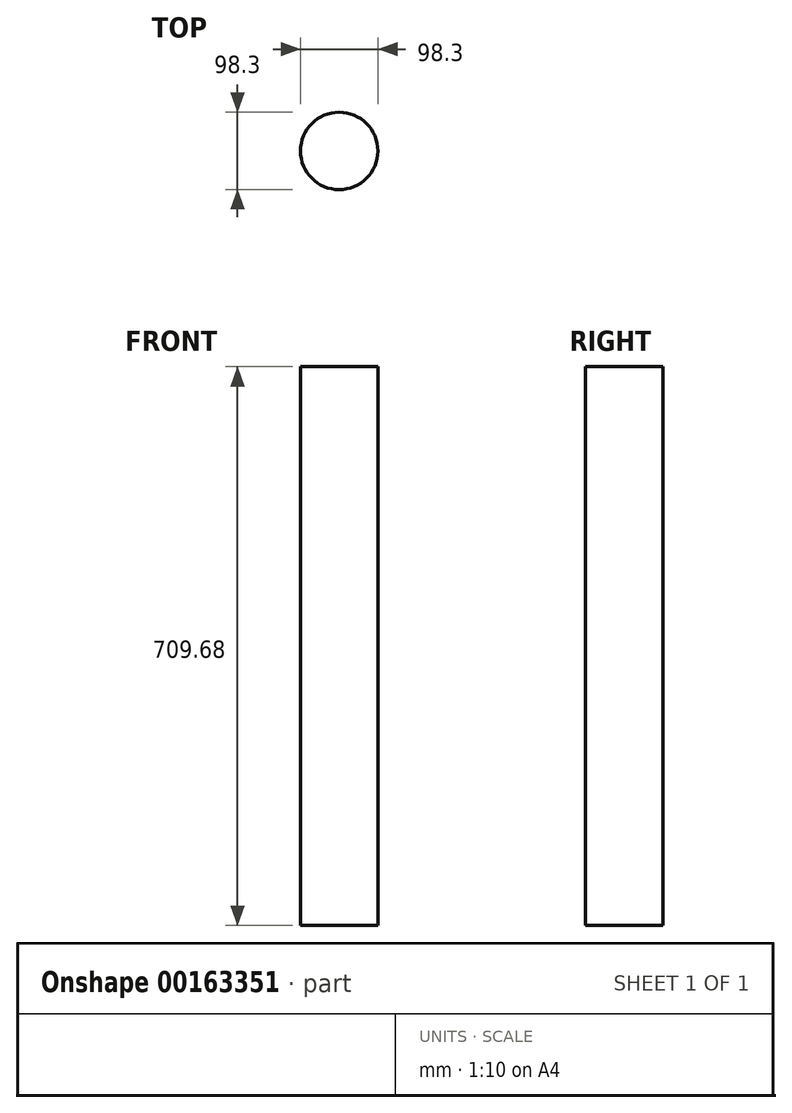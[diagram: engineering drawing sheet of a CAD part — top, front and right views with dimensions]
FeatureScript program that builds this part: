
annotation { "Feature Type Name" : "Feature", "Feature Type Description" : "" }
export const myFeature = defineFeature(function(context is Context, id is Id, definition is map)
    precondition{}
    {
        {
            var Q0;
            Q0=qCreatedBy(makeId("Top.planeOp"),FACE);
            var sketch = newSketch(context, id + "F0", { "sketchPlane" : qUnion([Q0])});
            skCircle(sketch, "E0", {"center": v(0, 0) * mm, "radius": 49.15 * mm});
            skSolve(sketch);
        }
        {
            var Q0;
            Q0=makeQuery(id+"F0.imprint","IMPRINT",FACE,{"disambiguationData":[TD([[makeQuery(id+"F0.imprint","IMPRINT",EDGE,{"derivedFrom":sQuery(id+"F0.wireOp",EDGE,"E0")}),1.0]])]});
            extrude(context, id + "F1", {"entities" : qUnion([Q0]), "depth" : 709.68 * mm});
        }
    });
